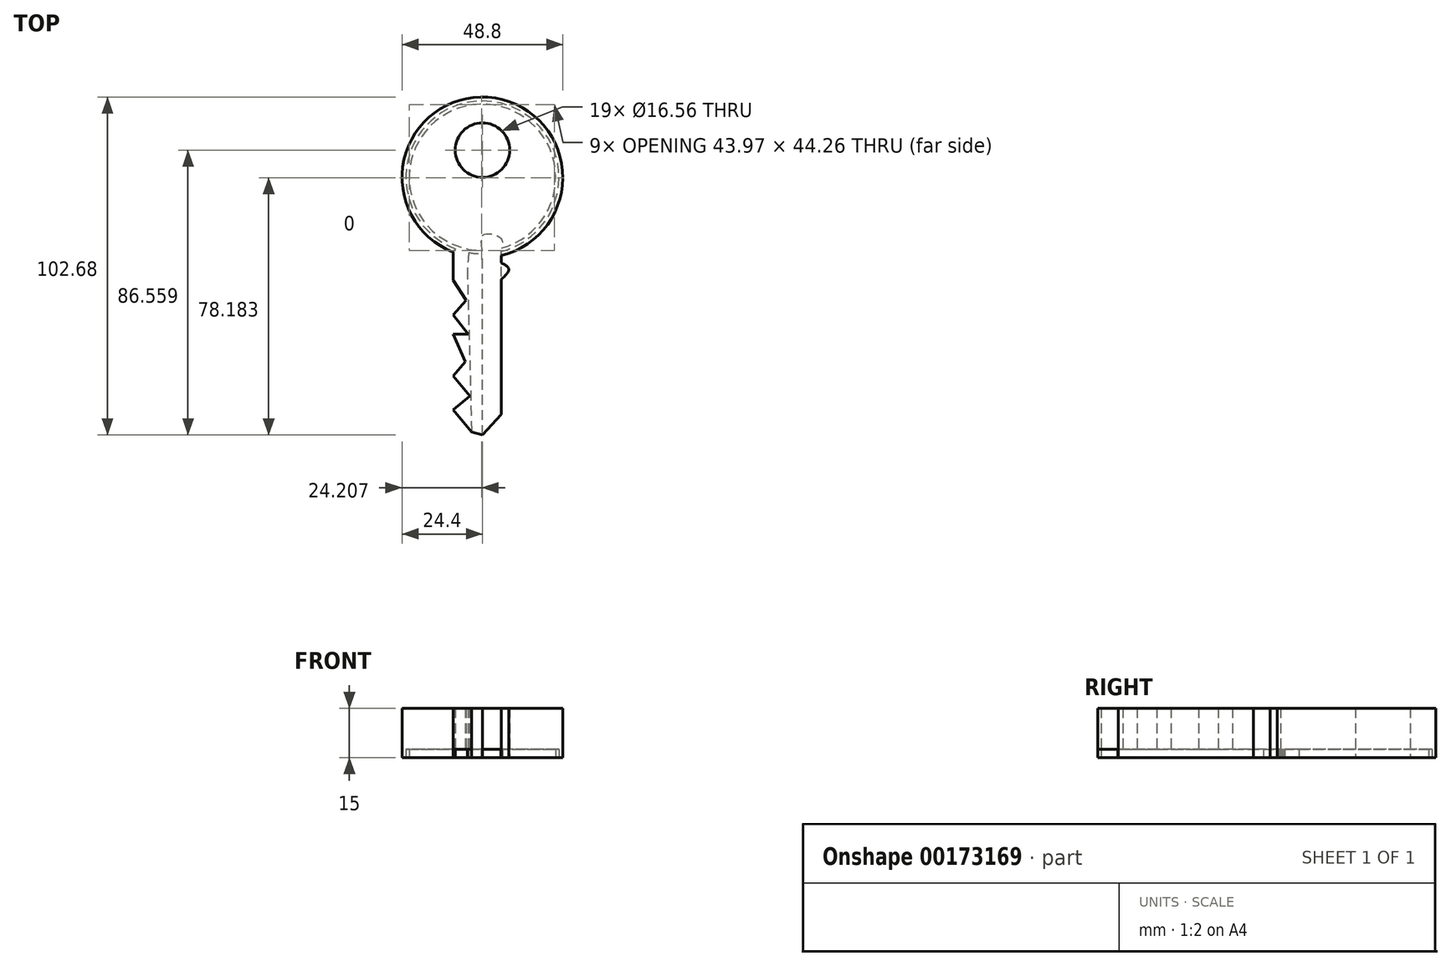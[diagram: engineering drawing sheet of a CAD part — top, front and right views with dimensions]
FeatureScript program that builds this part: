
annotation { "Feature Type Name" : "Feature", "Feature Type Description" : "" }
export const myFeature = defineFeature(function(context is Context, id is Id, definition is map)
    precondition{}
    {
        {
            var Q0;
            Q0=qCreatedBy(makeId("Top.planeOp"),FACE);
            var sketch = newSketch(context, id + "F0", { "sketchPlane" : qUnion([Q0])});
            skCircle(sketch, "E0", {"center": v(0, 36.19) * mm, "radius": 8.28 * mm});
            skLineSegment(sketch, "E1.right", {"start": v(8.84, 5.9) * mm, "end": v(8.84, 4.82) * mm});
            skLineSegment(sketch, "E2", {"start": v(5.69, -34.55) * mm, "end": v(5.63, -34.53) * mm});
            skPoint(sketch, "E3.3.internal.snap0", {"position": v(11.17, 2.41) * mm});
            skPoint(sketch, "E4.orphan", {"position": v(8.84, -47.65) * mm});
            skLineSegment(sketch, "E5", {"start": v(-8.99, 5.86) * mm, "end": v(-8.8, 5.86) * mm});
            skLineSegment(sketch, "E6", {"start": v(-8.9, 5.86) * mm, "end": v(-8.9, -3.37) * mm});
            skLineSegment(sketch, "E7", {"start": v(-3.28, -49.39) * mm, "end": v(-8.9, -42.69) * mm});
            skLineSegment(sketch, "E8", {"start": v(-8.9, -42.69) * mm, "end": v(-3.84, -38.46) * mm});
            skLineSegment(sketch, "E9", {"start": v(-3.84, -38.46) * mm, "end": v(-8.9, -32.43) * mm});
            skLineSegment(sketch, "E10", {"start": v(-8.9, -32.43) * mm, "end": v(-5.17, -28.1) * mm});
            skLineSegment(sketch, "E11", {"start": v(-5.17, -28.1) * mm, "end": v(-8.9, -19.7) * mm});
            skLineSegment(sketch, "E12", {"start": v(-8.9, -19.7) * mm, "end": v(-4.32, -19.7) * mm});
            skPoint(sketch, "E13.orphan", {"position": v(-8.9, 5.86) * mm});
            skLineSegment(sketch, "E14", {"start": v(0, -50.37) * mm, "end": v(5.69, -44.07) * mm});
            skLineSegment(sketch, "E15", {"start": v(5.69, -44.07) * mm, "end": v(5.69, -3.07) * mm});
            skPoint(sketch, "E16.center.orphan", {"position": v(0, 135.63) * mm});
            skPoint(sketch, "E3.1.internal.orphan", {"position": v(13.5, 0) * mm});
            skPoint(sketch, "E3.3.internal.orphan", {"position": v(11.17, 6.09) * mm});
            skPoint(sketch, "E17.end.orphan", {"position": v(8.84, -21.42) * mm});
            skPoint(sketch, "E18.orphan", {"position": v(2.33, -51.17) * mm});
            skPoint(sketch, "E19.orphan", {"position": v(-8.9, -47.6) * mm});
            skLineSegment(sketch, "E20", {"start": v(0, -50.37) * mm, "end": v(-3.28, -49.39) * mm});
            skArc(sketch, "E21", {"start": v(5.69, 4.18) * mm, "mid": v(1.68, 52.25) * mm, "end": v(-8.9, 5.18) * mm});
            skLineSegment(sketch, "E22", {"start": v(-8.9, -13.82) * mm, "end": v(-4.96, -9.47) * mm});
            skLineSegment(sketch, "E23", {"start": v(-4.96, -9.47) * mm, "end": v(-8.9, -3.37) * mm});
            skFitSpline(sketch, "E24", {"points": [v(5.69, 1.97) * mm, v(8, 0) * mm, v(5.69, -3.07) * mm], "startDerivative": vector(7.1, -3.8) * mm, "endDerivative": vector(-6.82, -6.23) * mm});
            skLineSegment(sketch, "E25.trimOffspring", {"start": v(5.69, 1.97) * mm, "end": v(5.69, 4.18) * mm});
            skLineSegment(sketch, "E26", {"start": v(-4.32, -19.7) * mm, "end": v(-8.9, -13.82) * mm});
            skSolve(sketch);
        }
        {
            var Q0;
            Q0=makeQuery(id+"F0.imprint","IMPRINT",FACE,{"disambiguationData":[TD([[makeQuery(id+"F0.imprint","IMPRINT",EDGE,{"derivedFrom":sQuery(id+"F0.wireOp",EDGE,"E0")}),-1.0]])]});
            extrude(context, id + "F1", {"entities" : qUnion([Q0]), "depth" : 15 * mm});
        }
        {
            var Q0;
            Q0=makeQuery(id+"F1.opExtrude","CAP_FACE",FACE,{"disambiguationData":[OSD([sQuery(id+"F0.wireOp",EDGE,"E0"),sQuery(id+"F0.wireOp",EDGE,"E6"),sQuery(id+"F0.wireOp",EDGE,"E7"),sQuery(id+"F0.wireOp",EDGE,"E8"),sQuery(id+"F0.wireOp",EDGE,"E9"),sQuery(id+"F0.wireOp",EDGE,"E10"),sQuery(id+"F0.wireOp",EDGE,"E11"),sQuery(id+"F0.wireOp",EDGE,"E12"),sQuery(id+"F0.wireOp",EDGE,"92a65fab-fcf9-45e2-b2ca-bde72a859c1a"),sQuery(id+"F0.wireOp",EDGE,"E14"),sQuery(id+"F0.wireOp",EDGE,"E15"),sQuery(id+"F0.wireOp",EDGE,"E20"),sQuery(id+"F0.wireOp",EDGE,"E21"),sQuery(id+"F0.wireOp",EDGE,"E22"),sQuery(id+"F0.wireOp",EDGE,"E23"),sQuery(id+"F0.wireOp",EDGE,"E24"),sQuery(id+"F0.wireOp",EDGE,"E25.trimOffspring")])],"isStart":true});
            var sketch = newSketch(context, id + "F2", { "sketchPlane" : qUnion([Q0])});
            skCircle(sketch, "E27", {"center": v(0, -27.9) * mm, "radius": 23.21 * mm});
            skCircle(sketch, "E28", {"center": v(0, -27.9) * mm, "radius": 22.23 * mm});
            skSolve(sketch);
        }
        {
            var Q0;
            Q0=makeQuery(id+"F2.imprint","IMPRINT",FACE,{"disambiguationData":[TD([[makeQuery(id+"F2.imprint","IMPRINT",EDGE,{"derivedFrom":sQuery(id+"F2.wireOp",EDGE,"E27")}),1.0]])]});
            extrude(context, id + "F3", {"entities" : qUnion([Q0]), "operationType" : NewBodyOperationType.REMOVE, "oppositeDirection" : true, "depth" : 2.5 * mm});
        }
        {
            var Q0;
            {var subQ0=sQuery(id+"F0.wireOp",EDGE,"E14");var subQ1=sQuery(id+"F0.wireOp",EDGE,"E25.trimOffspring");var subQ2=sQuery(id+"F0.wireOp",EDGE,"E12");var subQ3=sQuery(id+"F0.wireOp",EDGE,"E23");var subQ4=sQuery(id+"F0.wireOp",EDGE,"E11");var subQ5=sQuery(id+"F0.wireOp",EDGE,"E10");var subQ6=sQuery(id+"F0.wireOp",EDGE,"92a65fab-fcf9-45e2-b2ca-bde72a859c1a");var subQ7=sQuery(id+"F0.wireOp",EDGE,"E24");var subQ8=sQuery(id+"F0.wireOp",EDGE,"E6");var subQ9=sQuery(id+"F0.wireOp",EDGE,"E7");var subQ10=sQuery(id+"F0.wireOp",EDGE,"E15");var subQ11=sQuery(id+"F0.wireOp",EDGE,"E8");var subQ12=sQuery(id+"F0.wireOp",EDGE,"E9");var subQ13=sQuery(id+"F0.wireOp",EDGE,"E20");var subQ14=sQuery(id+"F0.wireOp",EDGE,"E21");var subQ15=sQuery(id+"F0.wireOp",EDGE,"E22");Q0=makeQuery(id+"F3.boolean.opBoolean","SPLIT",FACE,{"disambiguationData":[TD([makeQuery(id+"F1.opExtrude","SWEPT_FACE",FACE,{"disambiguationData":[OSD([subQ8])]})])],"derivedFrom":makeQuery(id+"F1.opExtrude","CAP_FACE",FACE,{"disambiguationData":[OSD([sQuery(id+"F0.wireOp",EDGE,"E0"),subQ8,subQ9,subQ11,subQ12,subQ5,subQ4,subQ2,subQ6,subQ0,subQ10,subQ13,subQ14,subQ15,subQ3,subQ7,subQ1])],"isStart":true})});}
            var sketch = newSketch(context, id + "F4", { "sketchPlane" : qUnion([Q0])});
            skLineSegment(sketch, "E29", {"start": v(5.57, -5.38) * mm, "end": v(5.57, 44.2) * mm});
            skLineSegment(sketch, "E30", {"start": v(5.57, 44.2) * mm, "end": v(2.84, 47.22) * mm});
            skLineSegment(sketch, "E31", {"start": v(2.84, 47.22) * mm, "end": v(0, 50.37) * mm});
            skLineSegment(sketch, "E32", {"start": v(0, 50.37) * mm, "end": v(0, -4.7) * mm});
            skFitSpline(sketch, "E33", {"points": [v(0, -4.7) * mm, v(0, -10.24) * mm, v(5.57, -9.42) * mm, v(5.57, -5.38) * mm], "startDerivative": vector(1.88, -15.36) * mm, "endDerivative": vector(-2.46, 15.73) * mm});
            skSolve(sketch);
        }
        {
            var Q0;
            Q0 = qSketchRegion(id + "F4", true);
            extrude(context, id + "F5", {"entities" : qUnion([Q0]), "operationType" : NewBodyOperationType.REMOVE, "oppositeDirection" : true, "depth" : 2.5 * mm});
        }
        {
            var Q0;
            {var subQ0=sQuery(id+"F0.wireOp",EDGE,"E14");var subQ1=sQuery(id+"F0.wireOp",EDGE,"E25.trimOffspring");var subQ2=sQuery(id+"F0.wireOp",EDGE,"E12");var subQ3=sQuery(id+"F0.wireOp",EDGE,"E23");var subQ4=sQuery(id+"F0.wireOp",EDGE,"E11");var subQ5=sQuery(id+"F0.wireOp",EDGE,"E10");var subQ6=sQuery(id+"F0.wireOp",EDGE,"92a65fab-fcf9-45e2-b2ca-bde72a859c1a");var subQ7=sQuery(id+"F0.wireOp",EDGE,"E24");var subQ8=sQuery(id+"F0.wireOp",EDGE,"E6");var subQ9=sQuery(id+"F0.wireOp",EDGE,"E7");var subQ10=sQuery(id+"F0.wireOp",EDGE,"E15");var subQ11=sQuery(id+"F0.wireOp",EDGE,"E8");var subQ12=sQuery(id+"F0.wireOp",EDGE,"E9");var subQ13=sQuery(id+"F0.wireOp",EDGE,"E20");var subQ14=sQuery(id+"F0.wireOp",EDGE,"E21");var subQ15=sQuery(id+"F0.wireOp",EDGE,"E22");Q0=makeQuery(id+"F3.boolean.opBoolean","SPLIT",FACE,{"disambiguationData":[TD([makeQuery(id+"F1.opExtrude","SWEPT_FACE",FACE,{"disambiguationData":[OSD([subQ8])]})])],"derivedFrom":makeQuery(id+"F1.opExtrude","CAP_FACE",FACE,{"disambiguationData":[OSD([sQuery(id+"F0.wireOp",EDGE,"E0"),subQ8,subQ9,subQ11,subQ12,subQ5,subQ4,subQ2,subQ6,subQ0,subQ10,subQ13,subQ14,subQ15,subQ3,subQ7,subQ1])],"isStart":true})});}
            var sketch = newSketch(context, id + "F6", { "sketchPlane" : qUnion([Q0])});
            skFitSpline(sketch, "E34", {"points": [v(-8.9, -5.18) * mm, v(-4.72, -9.81) * mm, v(-4.61, 0.1) * mm], "startDerivative": vector(10.5, -16.02) * mm, "endDerivative": vector(-1.95, 22.1) * mm});
            skLineSegment(sketch, "E35", {"start": v(-4.61, 0.1) * mm, "end": v(-3.28, 49.39) * mm});
            skSolve(sketch);
        }
        {
            var Q0;
            Q0 = qSketchRegion(id + "F6", true);
            var Q1;
            {var subQ4=sQuery(id+"F6.wireOp",EDGE,"E35");Q1=makeQuery(id+"F6.imprint","IMPRINT",FACE,{"disambiguationData":[TD([[makeQuery(id+"F6.imprint","IMPRINT",EDGE,{"derivedFrom":subQ4}),1.0]])]});}
            extrude(context, id + "F7", {"entities" : qUnion([Q0, Q1]), "operationType" : NewBodyOperationType.REMOVE, "oppositeDirection" : true, "depth" : 2.5 * mm});
        }
    });
